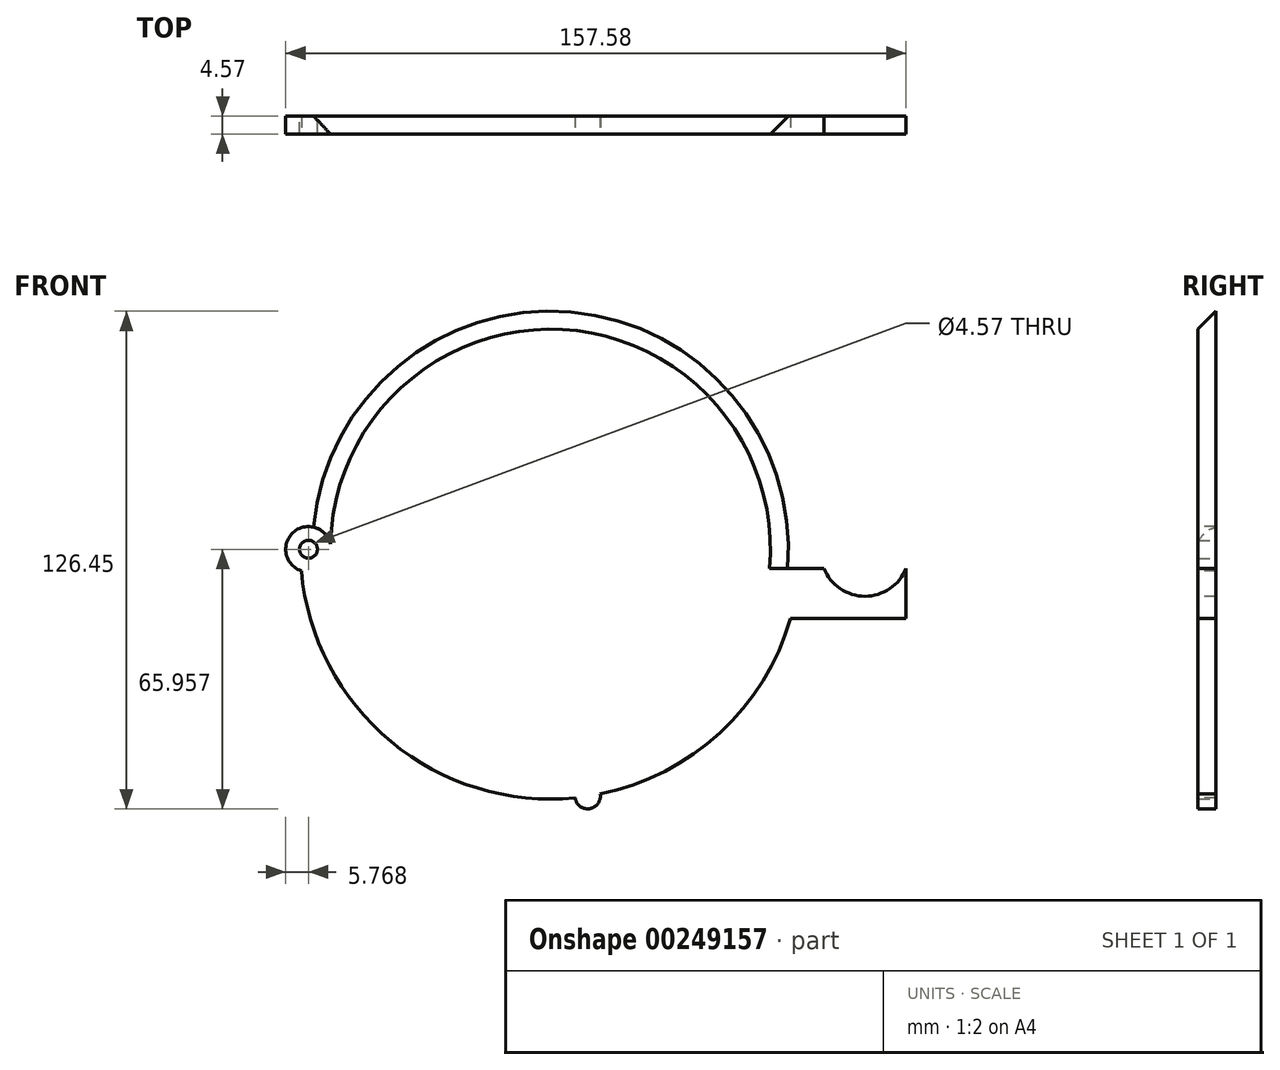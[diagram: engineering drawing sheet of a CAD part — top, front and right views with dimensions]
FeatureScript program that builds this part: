
annotation { "Feature Type Name" : "Feature", "Feature Type Description" : "" }
export const myFeature = defineFeature(function(context is Context, id is Id, definition is map)
    precondition{}
    {
        {
            var Q0;
            Q0=qCreatedBy(makeId("Front.planeOp"),FACE);
            var sketch = newSketch(context, id + "F0", { "sketchPlane" : qUnion([Q0])});
            skCircle(sketch, "E0", {"center": v(0, 0) * mm, "radius": 63.5 * mm});
            skSolve(sketch);
        }
        {
            var Q0;
            Q0=makeQuery(id+"F0.imprint","IMPRINT",FACE,{"disambiguationData":[TD([[makeQuery(id+"F0.imprint","IMPRINT",EDGE,{"derivedFrom":sQuery(id+"F0.wireOp",EDGE,"E0")}),1.0]])]});
            extrude(context, id + "F1", {"entities" : qUnion([Q0]), "depth" : 4.57 * mm});
        }
        {
            var Q0;
            Q0=makeQuery(id+"F01bwAH4B04rJDi_1.boolean.opBoolean","MERGE",FACE,{"derivedFrom":[makeQuery(id+"F1.opExtrude","CAP_FACE",FACE,{"disambiguationData":[OSD([sQuery(id+"F0.wireOp",EDGE,"E0")])],"isStart":false}),makeQuery(id+"F01bwAH4B04rJDi_1.opExtrude","SWEPT_FACE",FACE,{"disambiguationData":[OSD([sQuery(id+"FdWOhApfZtQyWu1_1.wireOp",EDGE,"53c49d9b-224d-4381-9111-b9742591b804.top")])]})]});
            var sketch = newSketch(context, id + "F2", { "sketchPlane" : qUnion([Q0])});
            skArc(sketch, "E1", {"start": v(6.28, -63.19) * mm, "mid": v(9.95, -65.97) * mm, "end": v(12.63, -62.23) * mm});
            skSolve(sketch);
        }
        {
            var Q0;
            {var subQ0=sQuery(id+"F2.wireOp",EDGE,"E1");Q0=makeQuery(id+"F2.imprint","IMPRINT",FACE,{"disambiguationData":[TD([[makeQuery(id+"F2.imprint","IMPRINT",EDGE,{"derivedFrom":subQ0}),1.0]])]});}
            extrude(context, id + "F3", {"entities" : qUnion([Q0]), "operationType" : NewBodyOperationType.ADD, "oppositeDirection" : true, "depth" : 4.57 * mm});
        }
        {
            var Q0;
            {var subQ0=sQuery(id+"F0.wireOp",EDGE,"E0");Q0=makeQuery(id+"F3.boolean.opBoolean","MERGE",FACE,{"derivedFrom":[makeQuery(id+"F01bwAH4B04rJDi_1.boolean.opBoolean","MERGE",FACE,{"derivedFrom":[makeQuery(id+"F1.opExtrude","CAP_FACE",FACE,{"disambiguationData":[OSD([subQ0])],"isStart":false}),makeQuery(id+"F01bwAH4B04rJDi_1.opExtrude","SWEPT_FACE",FACE,{"disambiguationData":[OSD([sQuery(id+"FdWOhApfZtQyWu1_1.wireOp",EDGE,"53c49d9b-224d-4381-9111-b9742591b804.top")])]})]}),makeQuery(id+"F3.opExtrude","CAP_FACE",FACE,{"disambiguationData":[OSD([subQ0,sQuery(id+"F2.wireOp",EDGE,"E1")])],"isStart":true})]});}
            var sketch = newSketch(context, id + "F4", { "sketchPlane" : qUnion([Q0])});
            skArc(sketch, "E2", {"start": v(-63.27, 5.43) * mm, "mid": v(-67.24, -0.05) * mm, "end": v(-63.26, -5.52) * mm});
            skSolve(sketch);
        }
        {
            var Q0;
            {var subQ0=sQuery(id+"F4.wireOp",EDGE,"E2");Q0=makeQuery(id+"F4.imprint","IMPRINT",FACE,{"disambiguationData":[TD([[makeQuery(id+"F4.imprint","IMPRINT",EDGE,{"derivedFrom":subQ0}),1.0]])]});}
            extrude(context, id + "F5", {"entities" : qUnion([Q0]), "operationType" : NewBodyOperationType.ADD, "oppositeDirection" : true, "depth" : 4.57 * mm});
        }
        {
            var Q0;
            {var subQ0=sQuery(id+"F0.wireOp",EDGE,"E0");Q0=makeQuery(id+"F5.boolean.opBoolean","MERGE",FACE,{"derivedFrom":[makeQuery(id+"F3.boolean.opBoolean","MERGE",FACE,{"derivedFrom":[makeQuery(id+"F1.opExtrude","CAP_FACE",FACE,{"disambiguationData":[OSD([subQ0])],"isStart":false}),makeQuery(id+"F3.opExtrude","CAP_FACE",FACE,{"disambiguationData":[OSD([subQ0,sQuery(id+"F2.wireOp",EDGE,"E1")])],"isStart":true})]}),makeQuery(id+"F5.opExtrude","CAP_FACE",FACE,{"disambiguationData":[OSD([subQ0,sQuery(id+"F4.wireOp",EDGE,"E2")])],"isStart":true})]});}
            var sketch = newSketch(context, id + "F6", { "sketchPlane" : qUnion([Q0])});
            skLineSegment(sketch, "E3.bottom", {"start": v(50.97, -4.9) * mm, "end": v(90.34, -4.9) * mm});
            skLineSegment(sketch, "E3.top", {"start": v(50.97, -17.6) * mm, "end": v(90.34, -17.6) * mm});
            skLineSegment(sketch, "E3.left", {"start": v(50.97, -4.9) * mm, "end": v(50.97, -17.6) * mm});
            skLineSegment(sketch, "E3.right", {"start": v(90.34, -4.9) * mm, "end": v(90.34, -17.6) * mm});
            skSolve(sketch);
        }
        {
            var Q0;
            {var subQ0=sQuery(id+"F6.wireOp",EDGE,"E3.right");Q0=makeQuery(id+"F6.imprint","IMPRINT",FACE,{"disambiguationData":[TD([[makeQuery(id+"F6.imprint","IMPRINT",EDGE,{"derivedFrom":subQ0}),-1.0]])]});}
            extrude(context, id + "F7", {"entities" : qUnion([Q0]), "operationType" : NewBodyOperationType.ADD, "oppositeDirection" : true, "depth" : 4.57 * mm});
        }
        {
            var Q0;
            {var subQ0=sQuery(id+"F0.wireOp",EDGE,"E0");Q0=makeQuery(id+"F7.boolean.opBoolean","MERGE",FACE,{"derivedFrom":[makeQuery(id+"F5.boolean.opBoolean","MERGE",FACE,{"derivedFrom":[makeQuery(id+"F3.boolean.opBoolean","MERGE",FACE,{"derivedFrom":[makeQuery(id+"F1.opExtrude","CAP_FACE",FACE,{"disambiguationData":[OSD([subQ0])],"isStart":false}),makeQuery(id+"F3.opExtrude","CAP_FACE",FACE,{"disambiguationData":[OSD([subQ0,sQuery(id+"F2.wireOp",EDGE,"E1")])],"isStart":true})]}),makeQuery(id+"F5.opExtrude","CAP_FACE",FACE,{"disambiguationData":[OSD([subQ0,sQuery(id+"F4.wireOp",EDGE,"E2")])],"isStart":true})]}),makeQuery(id+"F7.opExtrude","CAP_FACE",FACE,{"disambiguationData":[OSD([subQ0,sQuery(id+"F6.wireOp",EDGE,"E3.bottom"),sQuery(id+"F6.wireOp",EDGE,"E3.top"),sQuery(id+"F6.wireOp",EDGE,"E3.right")])],"isStart":true})]});}
            var sketch = newSketch(context, id + "F8", { "sketchPlane" : qUnion([Q0])});
            skArc(sketch, "E4", {"start": v(69.5, -4.9) * mm, "mid": v(79.92, -11.99) * mm, "end": v(90.34, -4.9) * mm});
            skSolve(sketch);
        }
        {
            var Q0;
            {var subQ0=sQuery(id+"F8.wireOp",EDGE,"E4");Q0=makeQuery(id+"F8.imprint","IMPRINT",FACE,{"disambiguationData":[TD([[makeQuery(id+"F8.imprint","IMPRINT",EDGE,{"derivedFrom":subQ0}),1.0]])]});}
            extrude(context, id + "F9", {"entities" : qUnion([Q0]), "operationType" : NewBodyOperationType.REMOVE, "oppositeDirection" : true, "depth" : 25.4 * mm});
        }
        {
            var Q0;
            {var subQ0=sQuery(id+"F0.wireOp",EDGE,"E0");Q0=makeQuery(id+"F7.boolean.opBoolean","MERGE",FACE,{"derivedFrom":[makeQuery(id+"F5.boolean.opBoolean","MERGE",FACE,{"derivedFrom":[makeQuery(id+"F3.boolean.opBoolean","MERGE",FACE,{"derivedFrom":[makeQuery(id+"F1.opExtrude","CAP_FACE",FACE,{"disambiguationData":[OSD([subQ0])],"isStart":true}),makeQuery(id+"F3.opExtrude","CAP_FACE",FACE,{"disambiguationData":[OSD([subQ0,sQuery(id+"F2.wireOp",EDGE,"E1")])],"isStart":false})]}),makeQuery(id+"F5.opExtrude","CAP_FACE",FACE,{"disambiguationData":[OSD([subQ0,sQuery(id+"F4.wireOp",EDGE,"E2")])],"isStart":false})]}),makeQuery(id+"F7.opExtrude","CAP_FACE",FACE,{"disambiguationData":[OSD([subQ0,sQuery(id+"F6.wireOp",EDGE,"E3.bottom"),sQuery(id+"F6.wireOp",EDGE,"E3.top"),sQuery(id+"F6.wireOp",EDGE,"E3.right")])],"isStart":false})]});}
            var sketch = newSketch(context, id + "F10", { "sketchPlane" : qUnion([Q0])});
            skCircle(sketch, "E5", {"center": v(61.47, -0.04) * mm, "radius": 2.29 * mm});
            skSolve(sketch);
        }
        {
            var Q0;
            Q0=makeQuery(id+"F10.imprint","IMPRINT",FACE,{"disambiguationData":[TD([[makeQuery(id+"F10.imprint","IMPRINT",EDGE,{"derivedFrom":sQuery(id+"F10.wireOp",EDGE,"E5")}),1.0]])]});
            extrude(context, id + "F11", {"entities" : qUnion([Q0]), "operationType" : NewBodyOperationType.REMOVE, "oppositeDirection" : true, "depth" : 25.4 * mm});
        }
        {
            var Q0;
            {var subQ0=sQuery(id+"F0.wireOp",EDGE,"E0");var subQ1=sQuery(id+"F4.wireOp",EDGE,"E2");Q0=makeQuery(id+"F7.boolean.opBoolean","SPLIT",EDGE,{"disambiguationData":[TD([makeQuery(id+"F5.opExtrude","SWEPT_FACE",FACE,{"disambiguationData":[OSD([subQ1])]})])],"derivedFrom":makeQuery(id+"F5.boolean.opBoolean","SPLIT",EDGE,{"disambiguationData":[OD(1.0)],"derivedFrom":makeQuery(id+"F1.opExtrude","CAP_EDGE",EDGE,{"disambiguationData":[OSD([subQ0])],"isStart":false})})});}
            chamfer(context, id + "F12", {"entities" : qUnion([Q0]), "width" : 7.62 * mm, "tangentPropagation" : true});
        }
    });
